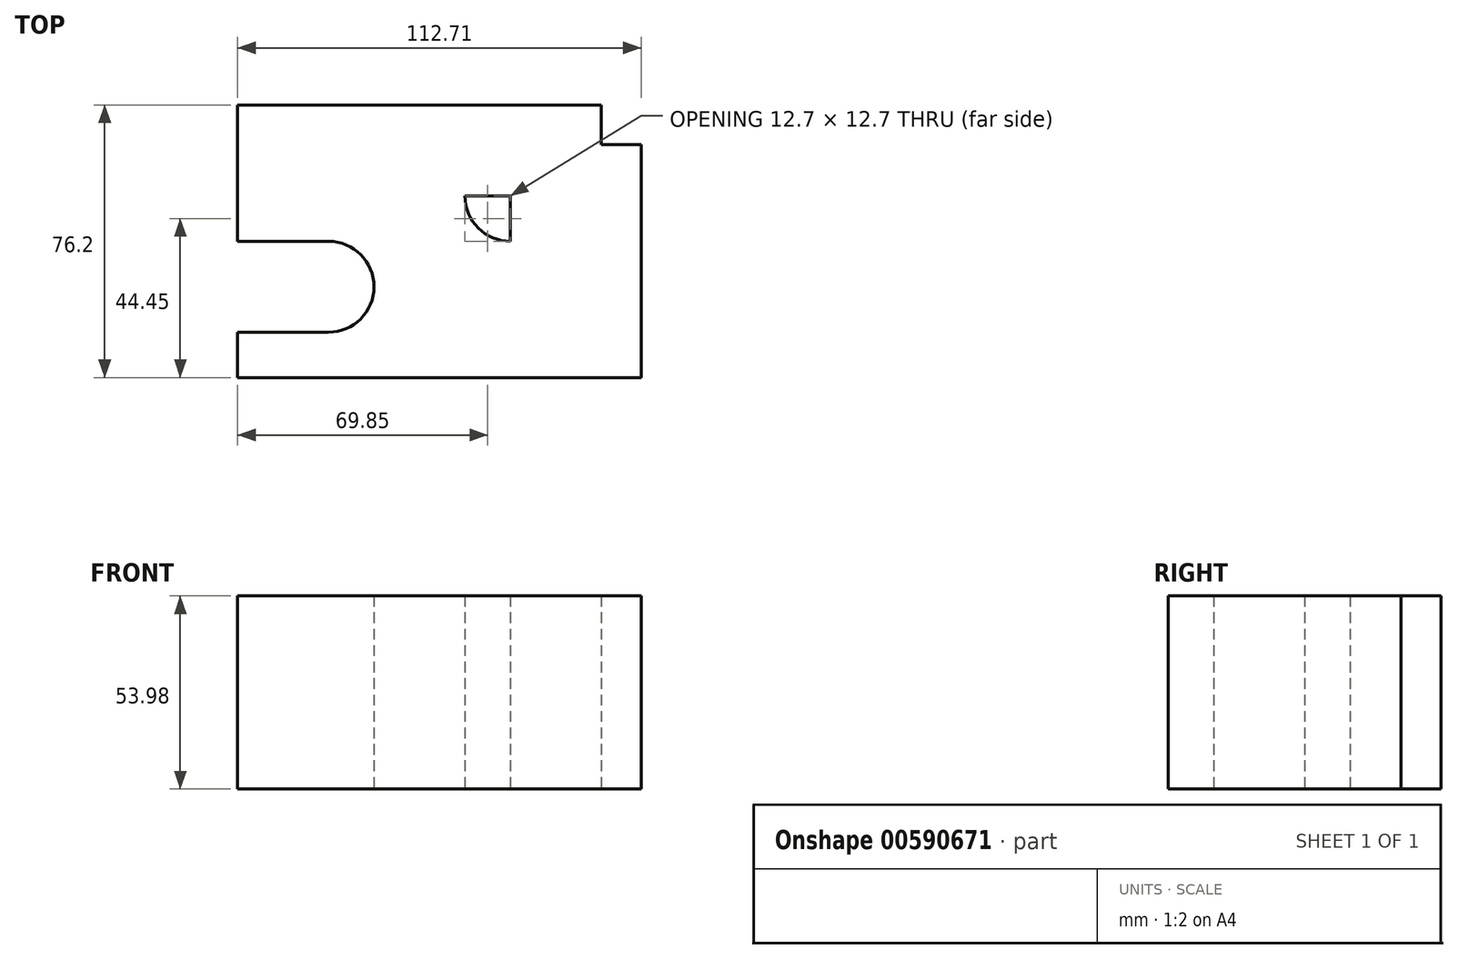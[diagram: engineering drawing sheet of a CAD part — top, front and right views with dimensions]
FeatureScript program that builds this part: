
annotation { "Feature Type Name" : "Feature", "Feature Type Description" : "" }
export const myFeature = defineFeature(function(context is Context, id is Id, definition is map)
    precondition{}
    {
        {
            var Q0;
            Q0=qCreatedBy(makeId("Top.planeOp"),FACE);
            var sketch = newSketch(context, id + "F0", { "sketchPlane" : qUnion([Q0])});
            skLineSegment(sketch, "E0.bottom", {"start": v(76.2, -50.8) * mm, "end": v(-76.2, -50.8) * mm});
            skLineSegment(sketch, "E0.top", {"start": v(76.2, 50.8) * mm, "end": v(-76.2, 50.8) * mm});
            skLineSegment(sketch, "E0.left", {"start": v(76.2, -50.8) * mm, "end": v(76.2, 50.8) * mm});
            skLineSegment(sketch, "E0.right", {"start": v(-76.2, -50.8) * mm, "end": v(-76.2, 50.8) * mm});
            skPoint(sketch, "E0.middle", {"position": v(0, 0) * mm});
            skLineSegment(sketch, "E1.bottom", {"start": v(-76.2, -38.1) * mm, "end": v(-50.8, -38.1) * mm});
            skLineSegment(sketch, "E1.top", {"start": v(-76.2, -12.7) * mm, "end": v(-50.8, -12.7) * mm});
            skLineSegment(sketch, "E1.left", {"start": v(-76.2, -38.1) * mm, "end": v(-76.2, -12.7) * mm});
            skLineSegment(sketch, "E1.right", {"start": v(-50.8, -38.1) * mm, "end": v(-50.8, -12.7) * mm});
            skCircle(sketch, "E2", {"center": v(-50.8, -25.4) * mm, "radius": 12.7 * mm});
            skLineSegment(sketch, "E3.bottom", {"start": v(-76.2, -50.8) * mm, "end": v(0, -50.8) * mm});
            skLineSegment(sketch, "E3.top", {"start": v(-76.2, 0) * mm, "end": v(0, 0) * mm});
            skLineSegment(sketch, "E3.left", {"start": v(-76.2, -50.8) * mm, "end": v(-76.2, 0) * mm});
            skLineSegment(sketch, "E3.right", {"start": v(0, -50.8) * mm, "end": v(0, 0) * mm});
            skCircle(sketch, "E4", {"center": v(0, 0) * mm, "radius": 12.7 * mm});
            skLineSegment(sketch, "E5.bottom", {"start": v(-76.2, -50.8) * mm, "end": v(36.51, -50.8) * mm});
            skLineSegment(sketch, "E5.top", {"start": v(-76.2, 25.4) * mm, "end": v(36.51, 25.4) * mm});
            skLineSegment(sketch, "E5.left", {"start": v(-76.2, -50.8) * mm, "end": v(-76.2, 25.4) * mm});
            skLineSegment(sketch, "E5.right", {"start": v(36.51, -50.8) * mm, "end": v(36.51, 25.4) * mm});
            skLineSegment(sketch, "E6.bottom", {"start": v(47.63, 14.29) * mm, "end": v(25.4, 14.29) * mm});
            skLineSegment(sketch, "E6.top", {"start": v(47.63, 36.51) * mm, "end": v(25.4, 36.51) * mm});
            skLineSegment(sketch, "E6.left", {"start": v(47.63, 14.29) * mm, "end": v(47.63, 36.51) * mm});
            skLineSegment(sketch, "E6.right", {"start": v(25.4, 14.29) * mm, "end": v(25.4, 36.51) * mm});
            skPoint(sketch, "E6.middle", {"position": v(36.51, 25.4) * mm});
            skSolve(sketch);
        }
        {
            var Q0;
            {var subQ5=sQuery(id+"F0.wireOp",EDGE,"E0.bottom");Q0=makeQuery(id+"F0.imprint","IMPRINT",FACE,{"disambiguationData":[TD([[makeQuery(id+"F0.imprint","IMPRINT",EDGE,{"derivedFrom":subQ5}),-1.0]])]});}
            var Q1;
            {var subQ2=sQuery(id+"F0.wireOp",EDGE,"E1.bottom");Q1=makeQuery(id+"F0.imprint","IMPRINT",FACE,{"disambiguationData":[TD([[makeQuery(id+"F0.imprint","IMPRINT",EDGE,{"derivedFrom":subQ2}),-1.0]])]});}
            var Q2;
            {var subQ7=sQuery(id+"F0.wireOp",EDGE,"E5.left");var subQ10=sQuery(id+"F0.wireOp",EDGE,"E3.top");var subQ11=makeQuery(id+"F0.imprint","INTERSECT",VERTEX,{"derivedFrom":[subQ10,subQ7]});Q2=makeQuery(id+"F0.imprint","IMPRINT",FACE,{"disambiguationData":[TD([[makeQuery(id+"F0.imprint","IMPRINT",EDGE,{"disambiguationData":[TD([[subQ11,-1.0]])],"derivedFrom":subQ10}),1.0]])]});}
            extrude(context, id + "F1", {"entities" : qUnion([Q0, Q1, Q2]), "depth" : 53.97 * mm, "offsetDistance" : 25.4 * mm});
        }
        {
            var Q0;
            Q0=makeQuery(id+"F1.opExtrude","SWEPT_FACE",FACE,{"disambiguationData":[OSD([sQuery(id+"F0.wireOp",EDGE,"E0.bottom"),sQuery(id+"F0.wireOp",EDGE,"E5.bottom")])]});
            var sketch = newSketch(context, id + "F2", { "sketchPlane" : qUnion([Q0])});
            skLineSegment(sketch, "E7.bottom", {"start": v(76.2, 53.98) * mm, "end": v(-76.2, 53.98) * mm});
            skLineSegment(sketch, "E7.top", {"start": v(76.2, 23.81) * mm, "end": v(-76.2, 23.81) * mm});
            skLineSegment(sketch, "E7.left", {"start": v(76.2, 53.98) * mm, "end": v(76.2, 23.81) * mm});
            skLineSegment(sketch, "E7.right", {"start": v(-76.2, 53.98) * mm, "end": v(-76.2, 23.81) * mm});
            skLineSegment(sketch, "E8", {"start": v(76.2, 53.98) * mm, "end": v(-76.2, 23.81) * mm});
            skSolve(sketch);
        }
        {
            var Q0;
            Q0=makeQuery(id+"F2.imprint","IMPRINT",FACE,{"disambiguationData":[TD([[makeQuery(id+"F2.imprint","IMPRINT",EDGE,{"derivedFrom":sQuery(id+"F2.wireOp",EDGE,"E7.bottom")}),1.0]])]});
            extrude(context, id + "F3", {"entities" : qUnion([Q0]), "operationType" : NewBodyOperationType.REMOVE, "oppositeDirection" : true, "depth" : 101.6 * mm, "offsetDistance" : 25.4 * mm});
        }
    });
